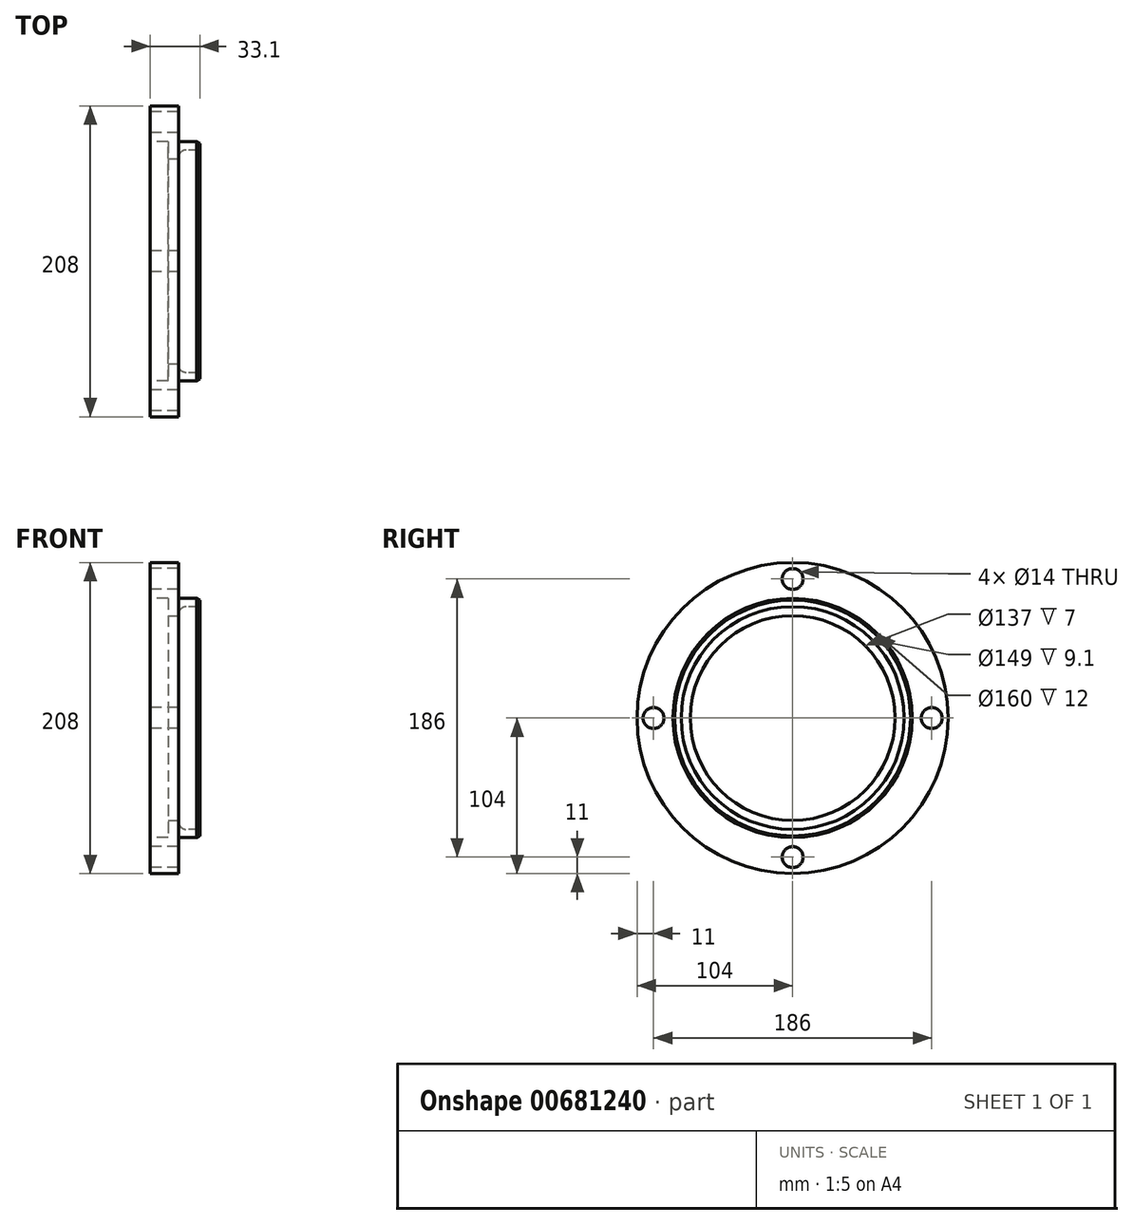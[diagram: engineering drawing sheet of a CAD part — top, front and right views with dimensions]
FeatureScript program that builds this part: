
annotation { "Feature Type Name" : "Feature", "Feature Type Description" : "" }
export const myFeature = defineFeature(function(context is Context, id is Id, definition is map)
    precondition{}
    {
        {
            var Q0;
            Q0=qCreatedBy(makeId("Right.planeOp"),FACE);
            var sketch = newSketch(context, id + "F0", { "sketchPlane" : qUnion([Q0])});
            skCircle(sketch, "E0", {"center": v(0, 0) * mm, "radius": 104 * mm});
            skCircle(sketch, "E1", {"center": v(0, 0) * mm, "radius": 68.5 * mm});
            skSolve(sketch);
        }
        {
            var Q0;
            Q0=qSketchRegion(id+"F0",true);
            extrude(context, id + "F1", {"entities" : qUnion([Q0]), "oppositeDirection" : true, "depth" : 19 * mm, "offsetDistance" : 25 * mm});
        }
        {
            var Q0;
            Q0=makeQuery(id+"F1.opExtrude","CAP_FACE",FACE,{"disambiguationData":[OSD([sQuery(id+"F0.wireOp",EDGE,"E0"),sQuery(id+"F0.wireOp",EDGE,"E1")])],"isStart":true});
            var sketch = newSketch(context, id + "F2", { "sketchPlane" : qUnion([Q0])});
            skCircle(sketch, "E2", {"center": v(0, 0) * mm, "radius": 80 * mm});
            skCircle(sketch, "E3", {"center": v(0, 0) * mm, "radius": 74.5 * mm});
            skSolve(sketch);
        }
        {
            var Q0;
            Q0=qSketchRegion(id+"F2",true);
            extrude(context, id + "F3", {"entities" : qUnion([Q0]), "operationType" : NewBodyOperationType.ADD, "depth" : 14.1 * mm, "offsetDistance" : 25 * mm});
        }
        {
            var Q0;
            Q0=makeQuery(id+"F1.opExtrude","CAP_FACE",FACE,{"disambiguationData":[OSD([sQuery(id+"F0.wireOp",EDGE,"E0"),sQuery(id+"F0.wireOp",EDGE,"E1")])],"isStart":false});
            var sketch = newSketch(context, id + "F4", { "sketchPlane" : qUnion([Q0])});
            skCircle(sketch, "E4", {"center": v(0, 0) * mm, "radius": 80 * mm});
            skSolve(sketch);
        }
        {
            var Q0;
            Q0=qSketchRegion(id+"F4",true);
            extrude(context, id + "F5", {"entities" : qUnion([Q0]), "operationType" : NewBodyOperationType.REMOVE, "oppositeDirection" : true, "depth" : 12 * mm, "offsetDistance" : 25 * mm});
        }
        {
            var Q0;
            Q0=makeQuery(id+"F3.opExtrude","CAP_EDGE",EDGE,{"disambiguationData":[OSD([sQuery(id+"F2.wireOp",EDGE,"E2")])],"isStart":false});
            chamfer(context, id + "F6", {"entities" : qUnion([Q0]), "chamferType" : ChamferType.OFFSET_ANGLE, "width" : 2 * mm, "oppositeDirection" : true, "angle" : 30 * degree, "tangentPropagation" : true});
        }
        {
            var Q0;
            Q0=makeQuery(id+"F3.opExtrude","CAP_EDGE",EDGE,{"disambiguationData":[OSD([sQuery(id+"F2.wireOp",EDGE,"E3")])],"isStart":true});
            fillet(context, id + "F7", {"entities" : qUnion([Q0]), "radius" : 5 * mm, "tangentPropagation" : true, "allowEdgeOverflow" : false});
        }
        {
            var Q0;
            Q0=makeQuery(id+"F1.opExtrude","CAP_FACE",FACE,{"disambiguationData":[OSD([sQuery(id+"F0.wireOp",EDGE,"E0"),sQuery(id+"F0.wireOp",EDGE,"E1")])],"isStart":false});
            var sketch = newSketch(context, id + "F8", { "sketchPlane" : qUnion([Q0])});
            skCircle(sketch, "E5", {"center": v(0, 0) * mm, "radius": 93 * mm, "construction": true});
            skLineSegment(sketch, "E6", {"start": v(0, 0) * mm, "end": v(0, -93) * mm, "construction": true});
            skPoint(sketch, "E7", {"position": v(0, -93) * mm});
            skPoint(sketch, "E8.1.0", {"position": v(93, 0) * mm});
            skPoint(sketch, "E8.2.0", {"position": v(0, 93) * mm});
            skPoint(sketch, "E8.3.0", {"position": v(-93, 0) * mm});
            skSolve(sketch);
        }
        {
            var Q0;
            Q0=sQuery(id+"F8.wireOp",VERTEX,"E7");
            var Q1;
            Q1=sQuery(id+"F8.wireOp",VERTEX,"E8.3.0");
            var Q2;
            Q2=sQuery(id+"F8.wireOp",VERTEX,"E8.2.0");
            var Q3;
            Q3=sQuery(id+"F8.wireOp",VERTEX,"E8.1.0");
            var Q4;
            Q4=makeQuery(id+"F1.opExtrude","SWEPT_BODY",BODY,{"disambiguationData":[OSD([sQuery(id+"F0.wireOp",EDGE,"E0"),sQuery(id+"F0.wireOp",EDGE,"E1")])]});
            hole(context, id + "F9", {"style" : HoleStyle.SIMPLE, "endStyle" : HoleEndStyle.BLIND, "standardTappedOrClearance" : lookupTablePath({ "standard" : "ISO", "size" : "14", "type" : "Drilled" }), "standardBlindInLast" : lookupTablePath({ "standard" : "ISO", "size" : "14", "type" : "Drilled" }), "holeDiameter" : 14 * mm, "majorDiameter" : 10 * mm, "holeDepth" : 25.5 * mm, "isTappedThrough" : true, "tappedDepth" : 21 * mm, "tapClearance" : 3, "locations" : qUnion([Q0, Q1, Q2, Q3]), "scope" : qUnion([Q4])});
        }
    });
